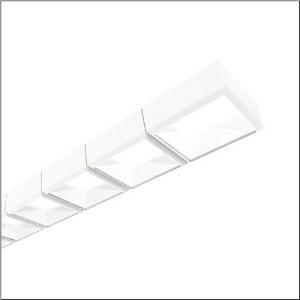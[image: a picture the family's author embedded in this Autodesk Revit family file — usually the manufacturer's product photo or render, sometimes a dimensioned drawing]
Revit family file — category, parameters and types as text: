
# Revit family: scriptus_11_5mz313d0twb
name_source: partatom
category: Lighting Fixtures
units: mm (PartAtom-declared; Revit-internal decimal feet)

## family parameters
Cut with Voids When Loaded = No
Host = Face
Light Source = No
Part Type = Normal
Room Calculation Point = No
Round Connector Dimension = Use Diameter
Shared = No

## types (1)
- --- (1 x LED 3000K+6500K / CRI = 80 (unbekannt), 3390 lm / 3550 lm, 3000K)
    Apparent Load = 107 VA
    CIE Flux Codes = 0 0 0 0 100 / 82 95 99 100 100
    Color Rendering = 80
    Color Temperature = 3000K
    Default Elevation = 1800 mm
    Description = Scriptus 11, office luminaire, primary optical cover: lenses, CAT 2 (L<= 3000cd/m²), light emission: direct/indirect distribution, primary light characteristic: symmetric, installation type: suspended mounting, LED, rated luminous flux: 13.880lm, luminous efficacy: 126lm/W, light colour: 8tw, colour temperature: 3000..6500K, control gear: DALI DT8, with terminal, 5-pole, mains connection: 230V, AC, 50Hz, rated input power: 110W, LED, control gear: ECG DALI, housing, luminaire housing, of aluminium, traffic white (RAL 9016), length: 2.648mm, width: 114mm, height: 57mm, protection rating (complete): IP20, insulation class (complete): insulation class I (protective earthing), certification: CE, protection symbol: F, permissible operating ambient temperature: <= +25°C, standard: EN 50419, packaging unit: 1 piece
    Height = 57 mm
    Lamp = 1 x LED 3000K+6500K / CRI >= 80 (unbekannt)
    Lamp Light Flux = 3390 lm / 3550 lm
    Lamp count = 1
    Length = 2648 mm
    Luminous efficacy = 130 lm/W
    Manufacturer = Siteco
    ModVariant = No
    Model = 5MZ313D0TWB
    Mounting Place = Ceiling
    Mounting Type = Pendant
    Number of Poles = 1
    OnlyDefault = Yes
    Power Factor = 1
    Product Name = Scriptus 11
    Product group = office luminaire | ceiling pendant
    ProductGroupID = 903
    Protection Class = Protection class I
    Protection Degree = IP 20
    RLX_Detail_Level = 1
    RLX_Emergency_Light_Flux = 0 lm
    RLX_Emergency_Type = 0
    RLX_Emergency_Type_DB = No
    RlxData = <blob elided: 31981 chars, md5=b8c24223>
    Socket = socket
    Standby Power = 0 W
    System Light Flux = 13880 lm
    System Power = 107 W
    Type Comments = individual setting: colour temperature 6500K
    Type Image = l_1004839.jpg
    URL = http://relux.com
    VarID = @adj_196180
    Voltage = 0 V
    Weight = 0.00 kg
    Width = 114 mm

## geometry (parser evidence)
native form markers: Blend x4, Sweep x18
no freeform markers — native parametric forms only
